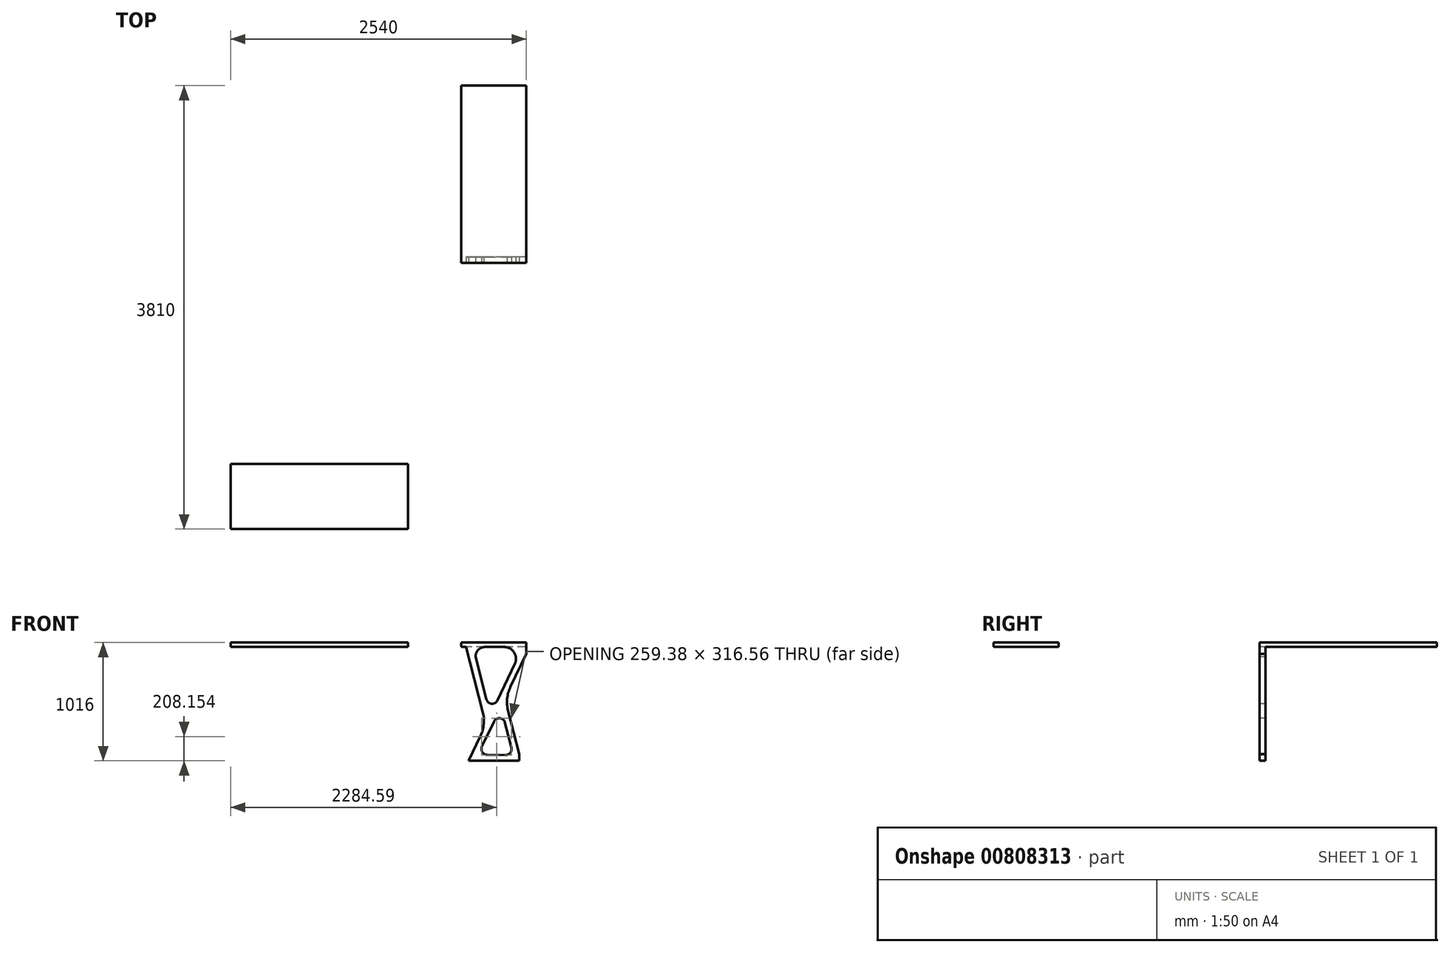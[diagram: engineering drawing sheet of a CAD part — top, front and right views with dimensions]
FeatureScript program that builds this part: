
annotation { "Feature Type Name" : "Feature", "Feature Type Description" : "" }
export const myFeature = defineFeature(function(context is Context, id is Id, definition is map)
    precondition{}
    {
        {
            var Q0;
            Q0=qCreatedBy(makeId("Top.planeOp"),FACE);
            var sketch = newSketch(context, id + "F0", { "sketchPlane" : qUnion([Q0])});
            skLineSegment(sketch, "E0.bottom", {"start": v(1270, 1625.6) * mm, "end": v(-1270, 1625.6) * mm});
            skLineSegment(sketch, "E0.top", {"start": v(-558.8, -1625.6) * mm, "end": v(-1270, -1625.6) * mm});
            skLineSegment(sketch, "E0.left", {"start": v(1270, 1625.6) * mm, "end": v(1270, 101.6) * mm});
            skLineSegment(sketch, "E0.right", {"start": v(-1270, 1625.6) * mm, "end": v(-1270, -1625.6) * mm});
            skPoint(sketch, "E0.middle", {"position": v(0, 0) * mm});
            skLineSegment(sketch, "E1.top", {"start": v(1244.6, -914.4) * mm, "end": v(-558.8, -914.4) * mm});
            skLineSegment(sketch, "E1.right", {"start": v(-558.8, -1625.6) * mm, "end": v(-558.8, -914.4) * mm});
            skLineSegment(sketch, "E2.bottom", {"start": v(-1270, 1168.4) * mm, "end": v(-635, 1168.4) * mm});
            skLineSegment(sketch, "E2.top", {"start": v(-1270, -101.6) * mm, "end": v(-635, -101.6) * mm});
            skLineSegment(sketch, "E2.left", {"start": v(-1270, 1168.4) * mm, "end": v(-1270, -101.6) * mm});
            skLineSegment(sketch, "E2.right", {"start": v(-635, 1168.4) * mm, "end": v(-635, -101.6) * mm});
            skPoint(sketch, "E1.bottom.start.orphan", {"position": v(1270, -1625.6) * mm});
            skLineSegment(sketch, "E3.bottom", {"start": v(-965.2, 1625.6) * mm, "end": v(-267.04, 1625.6) * mm});
            skLineSegment(sketch, "E3.top", {"start": v(-965.2, 1754.83) * mm, "end": v(-267.04, 1754.83) * mm});
            skLineSegment(sketch, "E3.left", {"start": v(-965.2, 1625.6) * mm, "end": v(-965.2, 1754.83) * mm});
            skLineSegment(sketch, "E3.right", {"start": v(-267.04, 1625.6) * mm, "end": v(-267.04, 1754.83) * mm});
            skLineSegment(sketch, "E4.top", {"start": v(1270, 101.6) * mm, "end": v(1244.6, 101.6) * mm});
            skLineSegment(sketch, "E4.right", {"start": v(1244.6, -914.4) * mm, "end": v(1244.6, 101.6) * mm});
            skLineSegment(sketch, "E5.bottom", {"start": v(267.04, 1625.6) * mm, "end": v(965.2, 1625.6) * mm});
            skLineSegment(sketch, "E5.top", {"start": v(267.04, 1754.83) * mm, "end": v(965.2, 1754.83) * mm});
            skLineSegment(sketch, "E5.left", {"start": v(267.04, 1625.6) * mm, "end": v(267.04, 1754.83) * mm});
            skLineSegment(sketch, "E5.right", {"start": v(965.2, 1625.6) * mm, "end": v(965.2, 1754.83) * mm});
            skSolve(sketch);
        }
        {
            var Q0;
            Q0=qCreatedBy(makeId("Top.planeOp"),FACE);
            cPlane(context, id + "F1", {"entities" : qUnion([Q0]), "cplaneType" : CPlaneType.OFFSET, "offset" : 1016 * mm, "width" : 152.4 * mm, "height" : 152.4 * mm});
        }
        {
            var Q0;
            Q0=qCreatedBy(id+"F1.planeOp",FACE);
            var sketch = newSketch(context, id + "F2", { "sketchPlane" : qUnion([Q0])});
            skLineSegment(sketch, "E6.0", {"start": v(-558.8, -1625.6) * mm, "end": v(-1270, -1625.6) * mm});
            skLineSegment(sketch, "E7.0", {"start": v(1270, 1625.6) * mm, "end": v(1270, 101.6) * mm});
            skLineSegment(sketch, "E8.0", {"start": v(1270, 1625.6) * mm, "end": v(711.2, 1625.6) * mm});
            skLineSegment(sketch, "E9.bottom", {"start": v(-1270, -1625.6) * mm, "end": v(254, -1625.6) * mm});
            skLineSegment(sketch, "E9.top", {"start": v(-1270, -2184.4) * mm, "end": v(254, -2184.4) * mm});
            skLineSegment(sketch, "E9.left", {"start": v(-1270, -1625.6) * mm, "end": v(-1270, -2184.4) * mm});
            skLineSegment(sketch, "E9.right", {"start": v(254, -1625.6) * mm, "end": v(254, -2184.4) * mm});
            skLineSegment(sketch, "E10.bottom", {"start": v(1270, 101.6) * mm, "end": v(711.2, 101.6) * mm});
            skLineSegment(sketch, "E10.left", {"start": v(1270, 101.6) * mm, "end": v(1270, 1625.6) * mm});
            skLineSegment(sketch, "E10.right", {"start": v(711.2, 101.6) * mm, "end": v(711.2, 1625.6) * mm});
            skPoint(sketch, "E11.orphan", {"position": v(-1270, 1625.6) * mm});
            skSolve(sketch);
        }
        {
            var Q0;
            Q0 = qSketchRegion(id + "F2", true);
            extrude(context, id + "F3", {"entities" : qUnion([Q0]), "oppositeDirection" : true, "depth" : 38.1 * mm, "offsetDistance" : 25.4 * mm});
        }
        {
            var Q0;
            Q0=makeQuery(id+"F3.opExtrude","SWEPT_FACE",FACE,{"disambiguationData":[OSD([sQuery(id+"F2.wireOp",EDGE,"E10.bottom")])]});
            var sketch = newSketch(context, id + "F4", { "sketchPlane" : qUnion([Q0])});
            skLineSegment(sketch, "E12", {"start": v(802.6, 0) * mm, "end": v(1224.36, 0) * mm});
            skLineSegment(sketch, "E13.0", {"start": v(1242.83, 979.97) * mm, "end": v(1241.85, 977.9) * mm});
            skLineSegment(sketch, "E14.0", {"start": v(1270, 919) * mm, "end": v(1134.3, 635.1) * mm});
            skLineSegment(sketch, "E15.0", {"start": v(752.63, 977.9) * mm, "end": v(896.33, 420.38) * mm});
            skLineSegment(sketch, "E16.0", {"start": v(833.84, 892.32) * mm, "end": v(927.61, 528.5) * mm});
            skArc(sketch, "E17", {"start": v(917, 977.9) * mm, "mid": v(857.33, 952.68) * mm, "end": v(833.84, 892.32) * mm});
            skLineSegment(sketch, "E18.trimOffspring", {"start": v(876.18, 212.86) * mm, "end": v(774.44, 0) * mm});
            skLineSegment(sketch, "E19.0", {"start": v(1244.6, 0) * mm, "end": v(-558.8, 0) * mm});
            skLineSegment(sketch, "E20", {"start": v(1270, 977.9) * mm, "end": v(1270, 919) * mm});
            skArc(sketch, "E21", {"start": v(1172.34, 832.49) * mm, "mid": v(1166.62, 930.48) * mm, "end": v(1080.68, 977.9) * mm});
            skArc(sketch, "E22", {"start": v(927.61, 528.5) * mm, "mid": v(971.9, 490.62) * mm, "end": v(1022.64, 519.28) * mm});
            skLineSegment(sketch, "E23.trimOffspring", {"start": v(1172.34, 832.49) * mm, "end": v(1022.64, 519.28) * mm});
            skLineSegment(sketch, "E24", {"start": v(1209.18, 58.9) * mm, "end": v(1114.15, 427.58) * mm});
            skLineSegment(sketch, "E25.0", {"start": v(1142.68, 113.35) * mm, "end": v(1087.22, 328.55) * mm});
            skArc(sketch, "E26", {"start": v(1087.22, 328.55) * mm, "mid": v(1042.93, 366.43) * mm, "end": v(992.2, 337.78) * mm});
            skArc(sketch, "E27", {"start": v(889.78, 123.5) * mm, "mid": v(892.64, 74.5) * mm, "end": v(935.6, 50.8) * mm});
            skArc(sketch, "E28", {"start": v(1093.5, 49.88) * mm, "mid": v(1133.65, 69.56) * mm, "end": v(1142.68, 113.35) * mm});
            skLineSegment(sketch, "E29", {"start": v(935.6, 50.8) * mm, "end": v(1093.5, 49.88) * mm});
            skLineSegment(sketch, "E30.trimOffspring", {"start": v(992.2, 337.78) * mm, "end": v(889.78, 123.5) * mm});
            skArc(sketch, "E31", {"start": v(876.18, 212.86) * mm, "mid": v(904.55, 314.85) * mm, "end": v(896.33, 420.38) * mm});
            skArc(sketch, "E32", {"start": v(1134.3, 635.1) * mm, "mid": v(1105.93, 533.12) * mm, "end": v(1114.15, 427.58) * mm});
            skLineSegment(sketch, "E33", {"start": v(1209.18, 0) * mm, "end": v(1209.18, 58.9) * mm});
            skLineSegment(sketch, "E34", {"start": v(917, 977.9) * mm, "end": v(1080.68, 977.9) * mm});
            skLineSegment(sketch, "E35.0", {"start": v(1270, 1016) * mm, "end": v(711.2, 1016) * mm});
            skLineSegment(sketch, "E36", {"start": v(711.2, 1016) * mm, "end": v(711.2, 977.9) * mm});
            skLineSegment(sketch, "E37", {"start": v(711.2, 977.9) * mm, "end": v(752.63, 977.9) * mm});
            skSolve(sketch);
        }
        {
            var Q0;
            Q0=makeQuery(id+"F4.imprint","IMPRINT",FACE,{"disambiguationData":[TD([[makeQuery(id+"F4.imprint","IMPRINT",EDGE,{"derivedFrom":sQuery(id+"F4.wireOp",EDGE,"E14.0")}),-1.0]])]});
            extrude(context, id + "F5", {"entities" : qUnion([Q0]), "operationType" : NewBodyOperationType.ADD, "oppositeDirection" : true, "depth" : 50.8 * mm, "offsetDistance" : 25.4 * mm});
        }
    });
